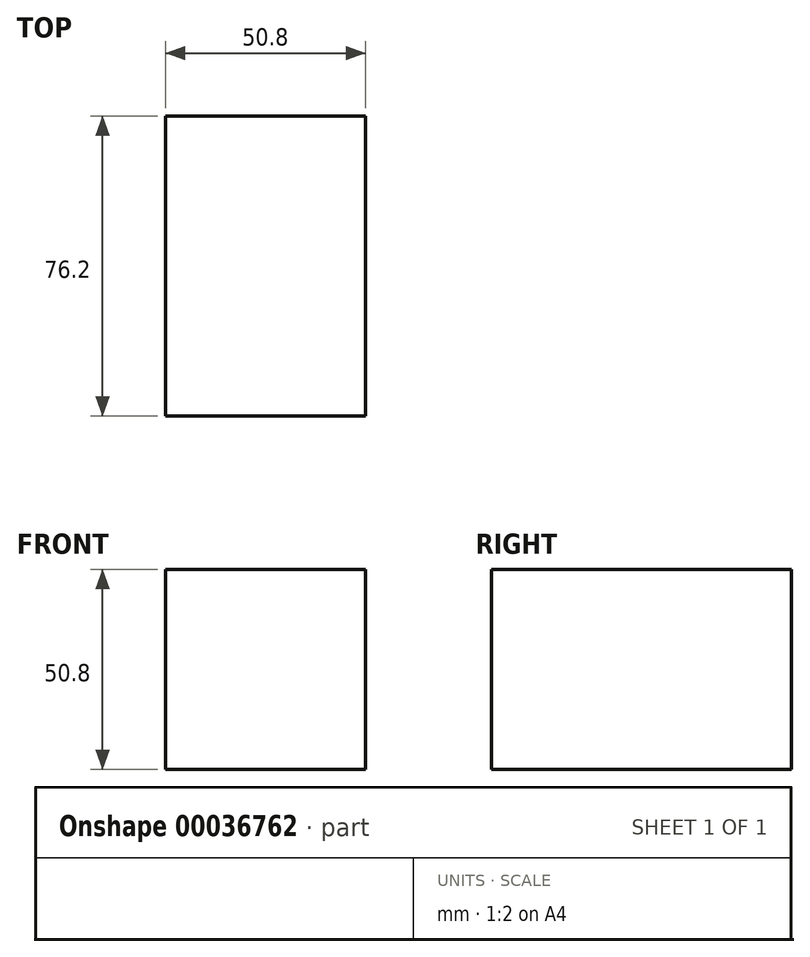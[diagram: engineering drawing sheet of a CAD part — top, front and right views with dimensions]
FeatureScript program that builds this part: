
annotation { "Feature Type Name" : "Feature", "Feature Type Description" : "" }
export const myFeature = defineFeature(function(context is Context, id is Id, definition is map)
    precondition{}
    {
        {
            var Q0;
            Q0=qCreatedBy(makeId("Front.planeOp"),FACE);
            var sketch = newSketch(context, id + "F0", { "sketchPlane" : qUnion([Q0])});
            skLineSegment(sketch, "E0.bottom", {"start": v(-33.03, 30.11) * mm, "end": v(17.77, 30.11) * mm});
            skLineSegment(sketch, "E0.top", {"start": v(-33.03, -20.69) * mm, "end": v(17.77, -20.69) * mm});
            skLineSegment(sketch, "E0.left", {"start": v(-33.03, 30.11) * mm, "end": v(-33.03, -20.69) * mm});
            skLineSegment(sketch, "E0.right", {"start": v(17.77, 30.11) * mm, "end": v(17.77, -20.69) * mm});
            skSolve(sketch);
        }
        {
            var Q0;
            Q0=makeQuery(id+"F0.imprint","IMPRINT",FACE,{"disambiguationData":[TD([[makeQuery(id+"F0.imprint","IMPRINT",EDGE,{"derivedFrom":sQuery(id+"F0.wireOp",EDGE,"E0.bottom")}),-1.0]])]});
            extrude(context, id + "F1", {"entities" : qUnion([Q0]), "depth" : 76.2 * mm});
        }
    });
